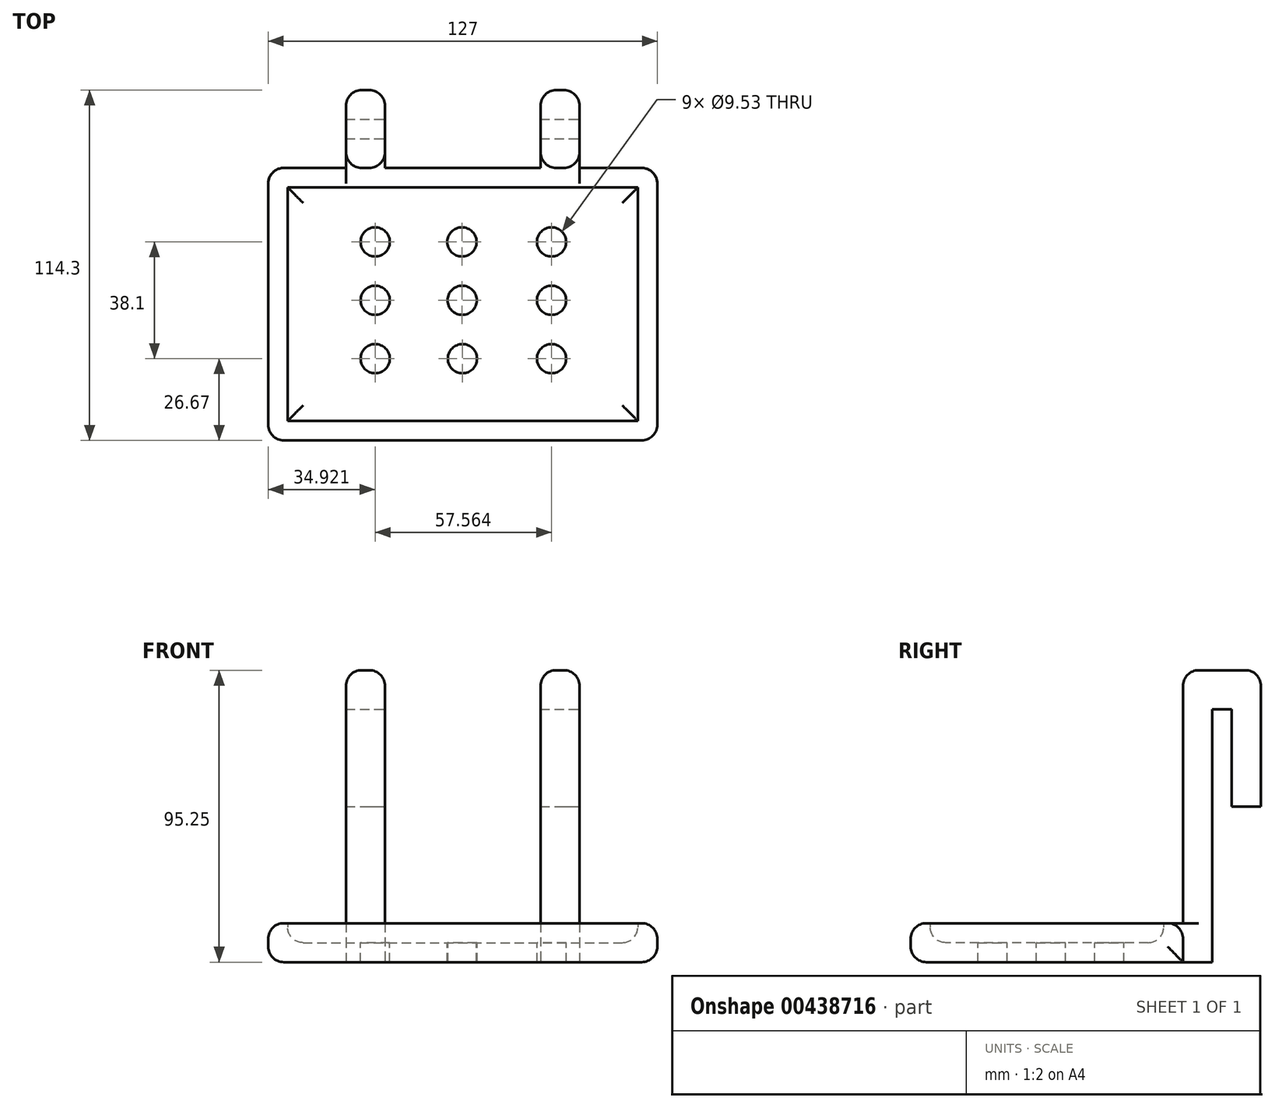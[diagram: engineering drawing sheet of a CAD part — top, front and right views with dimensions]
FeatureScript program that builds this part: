
annotation { "Feature Type Name" : "Feature", "Feature Type Description" : "" }
export const myFeature = defineFeature(function(context is Context, id is Id, definition is map)
    precondition{}
    {
        {
            var Q0;
            Q0=qCreatedBy(makeId("Front.planeOp"),FACE);
            var sketch = newSketch(context, id + "F0", { "sketchPlane" : qUnion([Q0])});
            skLineSegment(sketch, "E0.bottom", {"start": v(-45.38, 6.35) * mm, "end": v(81.62, 6.35) * mm});
            skLineSegment(sketch, "E0.top", {"start": v(-45.38, -6.35) * mm, "end": v(81.62, -6.35) * mm});
            skLineSegment(sketch, "E0.left", {"start": v(-45.38, 6.35) * mm, "end": v(-45.38, -6.35) * mm});
            skLineSegment(sketch, "E0.right", {"start": v(81.62, 6.35) * mm, "end": v(81.62, -6.35) * mm});
            skSolve(sketch);
        }
        {
            var Q0;
            Q0=makeQuery(id+"F0.imprint","IMPRINT",FACE,{"disambiguationData":[TD([[makeQuery(id+"F0.imprint","IMPRINT",EDGE,{"derivedFrom":sQuery(id+"F0.wireOp",EDGE,"E0.bottom")}),-1.0]])]});
            extrude(context, id + "F1", {"entities" : qUnion([Q0]), "depth" : 88.9 * mm});
        }
        {
            var Q0;
            Q0=qCreatedBy(makeId("Top.planeOp"),FACE);
            var sketch = newSketch(context, id + "F2", { "sketchPlane" : qUnion([Q0])});
            skLineSegment(sketch, "E1.bottom", {"start": v(-39.03, -6.35) * mm, "end": v(75.27, -6.35) * mm});
            skLineSegment(sketch, "E1.top", {"start": v(-39.03, -82.55) * mm, "end": v(75.27, -82.55) * mm});
            skLineSegment(sketch, "E1.left", {"start": v(-39.03, -6.35) * mm, "end": v(-39.03, -82.55) * mm});
            skLineSegment(sketch, "E1.right", {"start": v(75.27, -6.35) * mm, "end": v(75.27, -82.55) * mm});
            skSolve(sketch);
        }
        {
            var Q0;
            Q0 = qSketchRegion(id + "F2", true);
            var Q1;
            Q1=qCreatedBy(makeId("Top.planeOp"),FACE);
            extrude(context, id + "F3", {"entities" : qUnion([Q0]), "operationType" : NewBodyOperationType.REMOVE, "endBound" : BoundingType.UP_TO_NEXT, "endBoundEntityFace" : qUnion([Q1]), "depth" : 25.4 * mm});
        }
        {
            var Q0;
            Q0=qCreatedBy(makeId("Top.planeOp"),FACE);
            var sketch = newSketch(context, id + "F4", { "sketchPlane" : qUnion([Q0])});
            skLineSegment(sketch, "E2", {"start": v(-39.03, -43.18) * mm, "end": v(75.27, -43.18) * mm});
            skLineSegment(sketch, "E3", {"start": v(-39.03, -62.23) * mm, "end": v(75.27, -62.23) * mm});
            skLineSegment(sketch, "E4", {"start": v(-39.03, -24.13) * mm, "end": v(75.27, -24.13) * mm});
            skLineSegment(sketch, "E5", {"start": v(17.78, -6.35) * mm, "end": v(18.12, -82.55) * mm});
            skPoint(sketch, "E5.endSnap0", {"position": v(18.12, -19.05) * mm});
            skLineSegment(sketch, "E6", {"start": v(47.1, -6.35) * mm, "end": v(47.1, -82.55) * mm});
            skLineSegment(sketch, "E7", {"start": v(-10.46, -6.35) * mm, "end": v(-10.46, -82.55) * mm});
            skSolve(sketch);
        }
        {
            var Q0;
            Q0=qCreatedBy(makeId("Top.planeOp"),FACE);
            var sketch = newSketch(context, id + "F5", { "sketchPlane" : qUnion([Q0])});
            skCircle(sketch, "E8", {"center": v(-10.46, -24.13) * mm, "radius": 4.76 * mm});
            skCircle(sketch, "E9", {"center": v(17.85, -24.13) * mm, "radius": 4.76 * mm});
            skCircle(sketch, "E10", {"center": v(47.1, -24.13) * mm, "radius": 4.76 * mm});
            skCircle(sketch, "E11", {"center": v(-10.46, -43.18) * mm, "radius": 4.76 * mm});
            skCircle(sketch, "E12", {"center": v(17.94, -43.18) * mm, "radius": 4.76 * mm});
            skCircle(sketch, "E13", {"center": v(47.1, -43.18) * mm, "radius": 4.76 * mm});
            skCircle(sketch, "E14", {"center": v(-10.46, -62.23) * mm, "radius": 4.76 * mm});
            skCircle(sketch, "E15", {"center": v(18.02, -62.23) * mm, "radius": 4.76 * mm});
            skCircle(sketch, "E16", {"center": v(47.1, -62.23) * mm, "radius": 4.76 * mm});
            skSolve(sketch);
        }
        {
            var Q0;
            Q0 = qSketchRegion(id + "F5", true);
            extrude(context, id + "F6", {"entities" : qUnion([Q0]), "operationType" : NewBodyOperationType.REMOVE, "oppositeDirection" : true, "depth" : 6.35 * mm});
        }
        {
            var Q0;
            Q0=qCreatedBy(makeId("Front.planeOp"),FACE);
            var sketch = newSketch(context, id + "F7", { "sketchPlane" : qUnion([Q0])});
            skLineSegment(sketch, "E17.bottom", {"start": v(-19.98, 88.9) * mm, "end": v(-7.28, 88.9) * mm});
            skLineSegment(sketch, "E17.top", {"start": v(-19.98, -6.35) * mm, "end": v(-7.28, -6.35) * mm});
            skLineSegment(sketch, "E17.left", {"start": v(-19.98, 88.9) * mm, "end": v(-19.98, -6.35) * mm});
            skLineSegment(sketch, "E17.right", {"start": v(-7.28, 88.9) * mm, "end": v(-7.28, -6.35) * mm});
            skLineSegment(sketch, "E18.bottom", {"start": v(43.52, 88.9) * mm, "end": v(56.22, 88.9) * mm});
            skLineSegment(sketch, "E18.top", {"start": v(43.52, -6.35) * mm, "end": v(56.22, -6.35) * mm});
            skLineSegment(sketch, "E18.left", {"start": v(43.52, 88.9) * mm, "end": v(43.52, -6.35) * mm});
            skLineSegment(sketch, "E18.right", {"start": v(56.22, 88.9) * mm, "end": v(56.22, -6.35) * mm});
            skLineSegment(sketch, "E19", {"start": v(-19.98, 76.2) * mm, "end": v(-7.28, 76.2) * mm});
            skLineSegment(sketch, "E20", {"start": v(43.52, 76.2) * mm, "end": v(56.22, 76.2) * mm});
            skSolve(sketch);
        }
        {
            var Q0;
            Q0 = qSketchRegion(id + "F7", true);
            extrude(context, id + "F8", {"entities" : qUnion([Q0]), "operationType" : NewBodyOperationType.ADD, "depth" : -25.4 * mm});
        }
        {
            var Q0;
            Q0=qCreatedBy(makeId("Right.planeOp"),FACE);
            var sketch = newSketch(context, id + "F9", { "sketchPlane" : qUnion([Q0])});
            skLineSegment(sketch, "E21", {"start": v(9.53, -6.35) * mm, "end": v(9.53, 76.2) * mm});
            skLineSegment(sketch, "E22", {"start": v(9.53, 76.2) * mm, "end": v(15.87, 76.2) * mm});
            skLineSegment(sketch, "E23", {"start": v(15.87, 76.2) * mm, "end": v(15.88, 44.45) * mm});
            skLineSegment(sketch, "E24", {"start": v(15.88, 44.45) * mm, "end": v(25.4, 44.45) * mm});
            skLineSegment(sketch, "E25", {"start": v(25.4, 44.45) * mm, "end": v(25.4, -6.35) * mm});
            skLineSegment(sketch, "E26", {"start": v(25.4, -6.35) * mm, "end": v(9.53, -6.35) * mm});
            skSolve(sketch);
        }
        {
            var Q0;
            Q0 = qSketchRegion(id + "F9", true);
            extrude(context, id + "F10", {"entities" : qUnion([Q0]), "operationType" : NewBodyOperationType.REMOVE, "endBound" : BoundingType.SYMMETRIC, "oppositeDirection" : true, "depth" : 152.4 * mm});
        }
        {
            var Q0;
            Q0=makeQuery(id+"F1.opExtrude","CAP_EDGE",EDGE,{"disambiguationData":[OSD([sQuery(id+"F0.wireOp",EDGE,"E0.left")])],"isStart":false});
            var Q1;
            Q1=makeQuery(id+"F1.opExtrude","CAP_EDGE",EDGE,{"disambiguationData":[OSD([sQuery(id+"F0.wireOp",EDGE,"E0.right")])],"isStart":false});
            var Q2;
            Q2=makeQuery(id+"F1.opExtrude","CAP_EDGE",EDGE,{"disambiguationData":[OSD([sQuery(id+"F0.wireOp",EDGE,"E0.right")])],"isStart":true});
            var Q3;
            Q3=makeQuery(id+"F1.opExtrude","CAP_EDGE",EDGE,{"disambiguationData":[OSD([sQuery(id+"F0.wireOp",EDGE,"E0.left")])],"isStart":true});
            var Q4;
            Q4=makeQuery(id+"F8.opExtrude","CAP_EDGE",EDGE,{"disambiguationData":[OSD([sQuery(id+"F7.wireOp",EDGE,"E17.bottom")])],"isStart":true});
            var Q5;
            Q5=makeQuery(id+"F8.opExtrude","CAP_EDGE",EDGE,{"disambiguationData":[OSD([sQuery(id+"F7.wireOp",EDGE,"E17.bottom")])],"isStart":false});
            var Q6;
            Q6=makeQuery(id+"F8.opExtrude","CAP_EDGE",EDGE,{"disambiguationData":[OSD([sQuery(id+"F7.wireOp",EDGE,"E18.bottom")])],"isStart":true});
            var Q7;
            Q7=makeQuery(id+"F8.opExtrude","CAP_EDGE",EDGE,{"disambiguationData":[OSD([sQuery(id+"F7.wireOp",EDGE,"E18.bottom")])],"isStart":false});
            var Q8;
            Q8=makeQuery(id+"F1.opExtrude","SWEPT_EDGE",EDGE,{"disambiguationData":[OSD([sQuery(id+"F0.wireOp",EDGE,"E0.top"),sQuery(id+"F0.wireOp",EDGE,"E0.right")])]});
            var Q9;
            Q9=makeQuery(id+"F1.opExtrude","CAP_EDGE",EDGE,{"disambiguationData":[OSD([sQuery(id+"F0.wireOp",EDGE,"E0.top")])],"isStart":false});
            var Q10;
            Q10=makeQuery(id+"F1.opExtrude","SWEPT_EDGE",EDGE,{"disambiguationData":[OSD([sQuery(id+"F0.wireOp",EDGE,"E0.top"),sQuery(id+"F0.wireOp",EDGE,"E0.left")])]});
            var Q11;
            Q11=makeQuery(id+"F6.boolean.opBoolean","COPY",EDGE,{"derivedFrom":makeQuery(id+"F6.opExtrude","CAP_EDGE",EDGE,{"disambiguationData":[OSD([sQuery(id+"F5.wireOp",EDGE,"E11")])],"isStart":true})});
            var Q12;
            Q12=makeQuery(id+"F6.boolean.opBoolean","COPY",EDGE,{"derivedFrom":makeQuery(id+"F6.opExtrude","CAP_EDGE",EDGE,{"disambiguationData":[OSD([sQuery(id+"F5.wireOp",EDGE,"E14")])],"isStart":true})});
            var Q13;
            Q13=makeQuery(id+"F6.boolean.opBoolean","COPY",EDGE,{"derivedFrom":makeQuery(id+"F6.opExtrude","CAP_EDGE",EDGE,{"disambiguationData":[OSD([sQuery(id+"F5.wireOp",EDGE,"E8")])],"isStart":true})});
            var Q14;
            Q14=makeQuery(id+"F6.boolean.opBoolean","COPY",EDGE,{"derivedFrom":makeQuery(id+"F6.opExtrude","CAP_EDGE",EDGE,{"disambiguationData":[OSD([sQuery(id+"F5.wireOp",EDGE,"E9")])],"isStart":true})});
            var Q15;
            Q15=makeQuery(id+"F6.boolean.opBoolean","COPY",EDGE,{"derivedFrom":makeQuery(id+"F6.opExtrude","CAP_EDGE",EDGE,{"disambiguationData":[OSD([sQuery(id+"F5.wireOp",EDGE,"E12")])],"isStart":true})});
            var Q16;
            Q16=makeQuery(id+"F6.boolean.opBoolean","COPY",EDGE,{"derivedFrom":makeQuery(id+"F6.opExtrude","CAP_EDGE",EDGE,{"disambiguationData":[OSD([sQuery(id+"F5.wireOp",EDGE,"E15")])],"isStart":true})});
            var Q17;
            Q17=makeQuery(id+"F6.boolean.opBoolean","COPY",EDGE,{"derivedFrom":makeQuery(id+"F6.opExtrude","CAP_EDGE",EDGE,{"disambiguationData":[OSD([sQuery(id+"F5.wireOp",EDGE,"E10")])],"isStart":true})});
            var Q18;
            Q18=makeQuery(id+"F6.boolean.opBoolean","COPY",EDGE,{"derivedFrom":makeQuery(id+"F6.opExtrude","CAP_EDGE",EDGE,{"disambiguationData":[OSD([sQuery(id+"F5.wireOp",EDGE,"E13")])],"isStart":true})});
            var Q19;
            Q19=makeQuery(id+"F6.boolean.opBoolean","COPY",EDGE,{"derivedFrom":makeQuery(id+"F6.opExtrude","CAP_EDGE",EDGE,{"disambiguationData":[OSD([sQuery(id+"F5.wireOp",EDGE,"E16")])],"isStart":true})});
            var Q20;
            Q20=makeQuery(id+"F8.opExtrude","CAP_EDGE",EDGE,{"disambiguationData":[OSD([sQuery(id+"F7.wireOp",EDGE,"E18.left")])],"isStart":false});
            var Q21;
            Q21=makeQuery(id+"F8.opExtrude","CAP_EDGE",EDGE,{"disambiguationData":[OSD([sQuery(id+"F7.wireOp",EDGE,"E18.right")])],"isStart":false});
            var Q22;
            Q22=makeQuery(id+"F8.opExtrude","CAP_EDGE",EDGE,{"disambiguationData":[OSD([sQuery(id+"F7.wireOp",EDGE,"E17.right")])],"isStart":false});
            var Q23;
            Q23=makeQuery(id+"F8.opExtrude","CAP_EDGE",EDGE,{"disambiguationData":[OSD([sQuery(id+"F7.wireOp",EDGE,"E17.left")])],"isStart":false});
            fillet(context, id + "F11", {"entities" : qUnion([Q0, Q1, Q2, Q3, Q4, Q5, Q6, Q7, Q8, Q9, Q10, Q11, Q12, Q13, Q14, Q15, Q16, Q17, Q18, Q19, Q20, Q21, Q22, Q23]), "radius" : 5.08 * mm, "tangentPropagation" : true, "allowEdgeOverflow" : false});
        }
        {
            var Q0;
            Q0=makeQuery(id+"F8.opExtrude","SWEPT_EDGE",EDGE,{"disambiguationData":[OSD([sQuery(id+"F7.wireOp",EDGE,"E17.bottom"),sQuery(id+"F7.wireOp",EDGE,"E17.left")])]});
            var Q1;
            Q1=makeQuery(id+"F8.opExtrude","SWEPT_EDGE",EDGE,{"disambiguationData":[OSD([sQuery(id+"F7.wireOp",EDGE,"E17.bottom"),sQuery(id+"F7.wireOp",EDGE,"E17.right")])]});
            var Q2;
            Q2=makeQuery(id+"F8.opExtrude","SWEPT_EDGE",EDGE,{"disambiguationData":[OSD([sQuery(id+"F7.wireOp",EDGE,"E18.bottom"),sQuery(id+"F7.wireOp",EDGE,"E18.left")])]});
            var Q3;
            Q3=makeQuery(id+"F8.opExtrude","SWEPT_EDGE",EDGE,{"disambiguationData":[OSD([sQuery(id+"F7.wireOp",EDGE,"E18.bottom"),sQuery(id+"F7.wireOp",EDGE,"E18.right")])]});
            fillet(context, id + "F12", {"entities" : qUnion([Q0, Q1, Q2, Q3]), "radius" : 5.08 * mm, "tangentPropagation" : true, "allowEdgeOverflow" : false});
        }
        {
            var Q0;
            Q0=makeQuery(id+"F3.boolean.opBoolean","COPY",EDGE,{"derivedFrom":makeQuery(id+"F3.opExtrude","CAP_EDGE",EDGE,{"disambiguationData":[OSD([sQuery(id+"F2.wireOp",EDGE,"E1.left")])],"isStart":true})});
            var Q1;
            Q1=makeQuery(id+"F3.boolean.opBoolean","COPY",EDGE,{"derivedFrom":makeQuery(id+"F3.opExtrude","CAP_EDGE",EDGE,{"disambiguationData":[OSD([sQuery(id+"F2.wireOp",EDGE,"E1.top")])],"isStart":true})});
            var Q2;
            Q2=makeQuery(id+"F3.boolean.opBoolean","COPY",EDGE,{"derivedFrom":makeQuery(id+"F3.opExtrude","CAP_EDGE",EDGE,{"disambiguationData":[OSD([sQuery(id+"F2.wireOp",EDGE,"E1.bottom")])],"isStart":true})});
            var Q3;
            Q3=makeQuery(id+"F3.boolean.opBoolean","COPY",EDGE,{"derivedFrom":makeQuery(id+"F3.opExtrude","CAP_EDGE",EDGE,{"disambiguationData":[OSD([sQuery(id+"F2.wireOp",EDGE,"E1.right")])],"isStart":true})});
            fillet(context, id + "F13", {"entities" : qUnion([Q0, Q1, Q2, Q3]), "radius" : 5.08 * mm, "tangentPropagation" : true, "allowEdgeOverflow" : false});
        }
        {
            var Q0;
            Q0=makeQuery(id+"F1.opExtrude","CAP_EDGE",EDGE,{"disambiguationData":[OSD([sQuery(id+"F0.wireOp",EDGE,"E0.bottom")])],"isStart":false});
            fillet(context, id + "F14", {"entities" : qUnion([Q0]), "radius" : 5.08 * mm, "tangentPropagation" : true, "allowEdgeOverflow" : false});
        }
    });
